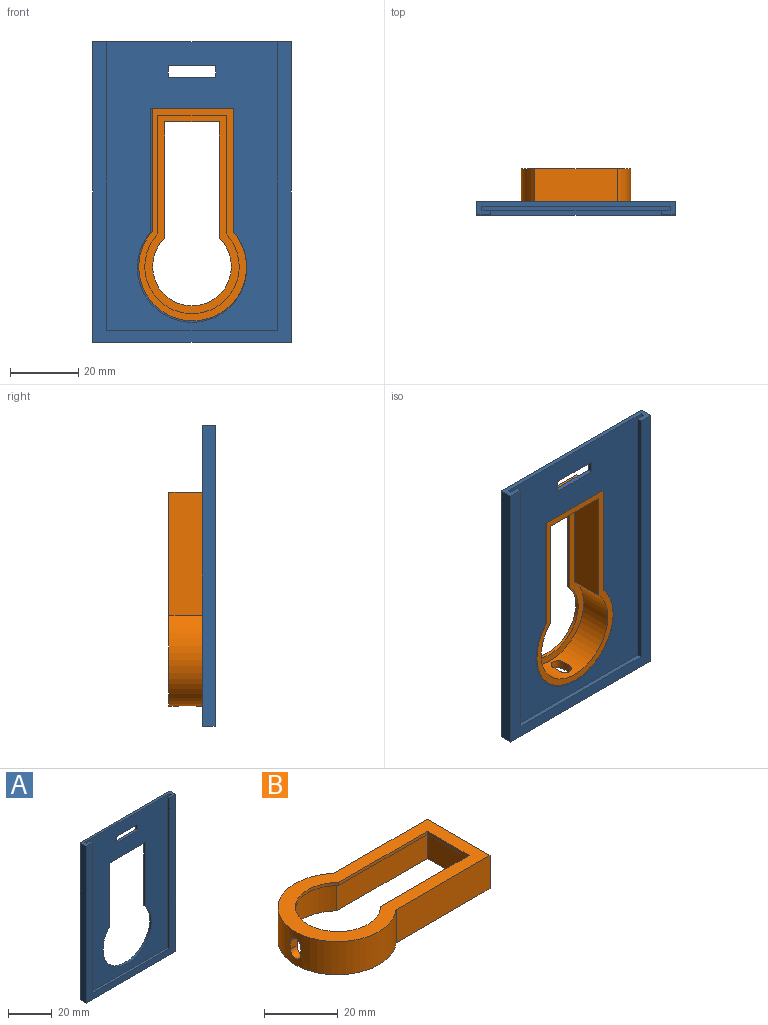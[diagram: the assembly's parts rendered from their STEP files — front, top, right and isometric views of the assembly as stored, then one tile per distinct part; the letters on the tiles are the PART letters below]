
ASSEMBLY  parts=2 mates=1
PART A: 22 faces, bbox 58x3.8x88 mm
  f0: plane 88x58mm, normal (0,1,0), area 3512.5mm2, adj f2,f4,f6,f7,f14,f15,f16,f17
  f1: plane 86.5x55mm, normal (0,-1,0), area 3166mm2, adj f2,f8,f9,f10,f14,f15,f16,f17
  f2: plane 58x3.8mm, normal (0,0,1), area 89.4mm2, adj f0,f1,f3,f4,f5,f6,f8,f9
  f3: plane 86.5x55mm, normal (0,1,0), area 532.5mm2, adj f2,f8,f9,f10,f11,f12,f13
  f4: plane 88x3.8mm, normal (-1,0,0), area 334.4mm2, adj f0,f2,f5,f7
  f5: plane 88x58mm, normal (0,-1,0), area 879mm2, adj f2,f4,f6,f7,f11,f12,f13
  f6: plane 88x3.8mm, normal (1,0,0), area 334.4mm2, adj f0,f2,f5,f7
  f7: plane 58x3.8mm, normal (0,0,-1), area 220.4mm2, adj f0,f4,f5,f6
  f8: plane 86.5x1.2mm, normal (-1,0,0), area 103.8mm2, adj f1,f2,f3,f10
  f9: plane 86.5x1.2mm, normal (1,0,0), area 103.8mm2, adj f1,f2,f3,f10
  f10: plane 55x1.2mm, normal (0,0,1), area 66mm2, adj f1,f3,f8,f9
  f11: plane 84.5x1.3mm, normal (1,0,0), area 109.8mm2, adj f2,f3,f5,f12
  f12: plane 50x1.3mm, normal (0,0,1), area 65mm2, adj f3,f5,f11,f13
  f13: plane 84.5x1.3mm, normal (-1,0,0), area 109.8mm2, adj f2,f3,f5,f12
  f14: plane 14x1.3mm, normal (0,0,1), area 18.2mm2, adj f0,f1,f15,f17
  f15: plane 3.5x1.3mm, normal (1,0,0), area 4.6mm2, adj f0,f1,f14,f16
  f16: plane 14x1.3mm, normal (0,0,-1), area 18.2mm2, adj f0,f1,f15,f17
  f17: plane 3.5x1.3mm, normal (-1,0,0), area 4.6mm2, adj f0,f1,f14,f16
  f18: cylinder r=15.75mm len=31.5mm, axis (0,1,0), area 93.9mm2, adj f0,f1,f19,f21
  f19: plane 36x1.3mm, normal (1,0,0), area 46.8mm2, adj f0,f1,f18,f20
  f20: plane 23.63x1.3mm, normal (0,0,-1), area 30.7mm2, adj f0,f1,f19,f21
  f21: plane 36x1.3mm, normal (-1,0,0), area 46.8mm2, adj f0,f1,f18,f20
PART B: 19 faces, bbox 62.6x32x11 mm
  f0: plane 34x1mm, normal (0,1,0), area 34mm2, adj f1,f3,f4,f14
  f1: plane 16x1mm, normal (-1,0,0), area 16mm2, adj f0,f2,f4,f14
  f2: plane 34x1mm, normal (0,-1,0), area 34mm2, adj f1,f3,f4,f14
  f3: cylinder r=11.5mm len=23mm, axis (0,0,1), area 54.6mm2, adj f0,f2,f4,f14
  f4: plane 62.57x32mm, normal (0,0,1), area 654.1mm2, adj f0,f1,f2,f3,f6,f7,f8,f9
  f5: plane 62.57x32mm, normal (0,0,-1), area 343.8mm2, adj f6,f7,f8,f9,f10,f11,f12,f13
  f6: plane 35.98x11mm, normal (0,1,0), area 395.8mm2, adj f4,f5,f7,f9
  f7: cylinder r=16mm len=32mm, axis (0,0,-1), area 783.5mm2, adj f4,f5,f6,f8,f15,f16,f17,f18
  f8: plane 36x11mm, normal (0,-1,0), area 396mm2, adj f4,f5,f7,f9
  f9: plane 24x11mm, normal (1,0,0), area 264mm2, adj f4,f5,f6,f8
  f10: plane 34.75x10mm, normal (0,1,0), area 347.5mm2, adj f5,f11,f13,f14
  f11: cylinder r=13.8mm len=27.6mm, axis (0,0,-1), area 619.5mm2, adj f5,f10,f12,f14,f15,f16,f17,f18
  f12: plane 34.75x10mm, normal (0,-1,0), area 347.5mm2, adj f5,f11,f13,f14
  f13: plane 20x10mm, normal (-1,0,0), area 200mm2, adj f5,f10,f12,f14
  f14: plane 58.06x27.6mm, normal (0,0,-1), area 310.2mm2, adj f0,f1,f2,f3,f10,f11,f12,f13
  f15: plane 2.8x2.53mm, normal (0,-1,0), area 7.1mm2, adj f7,f11,f16,f18
  f16: cylinder r=2mm len=4mm, axis (1,0,0), area 15.8mm2, adj f7,f11,f15,f17
  f17: plane 2.8x2.53mm, normal (0,1,0), area 7.1mm2, adj f7,f11,f16,f18
  f18: cylinder r=2mm len=4mm, axis (1,0,0), area 15.8mm2, adj f7,f11,f15,f17
PLACE A t=(8.6,11.43,13.29)mm
PLACE B rot(axis=(-0.58,-0.58,-0.58),120deg) t=(18.69,5.45,65.58)mm
MATE fastened B.f5 <-> A.f1  axis (0,1,0) through (26.04,5.45,81.77)mm
